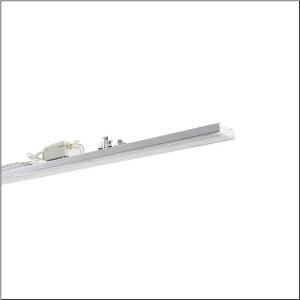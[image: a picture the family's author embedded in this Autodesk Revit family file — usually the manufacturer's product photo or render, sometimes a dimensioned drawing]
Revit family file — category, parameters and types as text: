
# Revit family: licross_r__21_recessed_ho_52te1ecn4cxs_0519
name_source: partatom
category: Lighting Fixtures
units: mm (PartAtom-declared; Revit-internal decimal feet)

## family parameters
Cut with Voids When Loaded = No
Host = Face
Light Source = No
Part Type = Normal
Room Calculation Point = No
Round Connector Dimension = Use Diameter
Shared = No

## types (1)
- --- (1 x LED, 12350 lm, 68.4 W, 4000K)
    Apparent Load = 68 VA
    CIE Flux Codes = 85 95 99 100 100
    Color Rendering = 80
    Color Temperature = 4000K
    Default Elevation = 1800 mm
    Description = Licross® 21 Recessed HO, luminaire insert, of sheet steel, galvanised, coil coated, white, length: 1.500mm, width: 66mm, height: 67mm, LED rated luminous flux: 12.350lm, light colour: 840, control gear: ON/OFF Multilumen, CLOi, control gear: ECG Multilumen, with plug, 3-pole, with phase selection, mains connection: 220..240V, AC, 50/60Hz, start of lifetime: 69W, end of service life: 83W, halogen-free wiring, primary light control with lens, of plastic, primary optical cover: cover, of PMMA, light emission: direct distribution, primary light characteristic: symmetric, protection rating (complete): IP54, insulation class (complete): insulation class I (protective earthing), certification: CE, ENEC, VDE, UKCA, protection symbol: D if used in an environment with non-conductive dust loads with corresponding accessories, impact resistance: IK06, permissible ambient temperature for indoor applications: -35..+30°C, corresponds to IFS (International Featured Standards) requirements for safety and quality in the food industry, reducing of maximum allowable ambient temperature of 5°C with ceiling mounting, LABS conformity tested according to VDMA 24364:2018-05, packaging unit: 1 piece
    Height = 58 mm
    Lamp = 1 x LED
    Lamp Light Flux = 12350 lm
    Lamp Power = 68.4 W
    Lamp count = 1
    Length = 1500 mm
    Luminous efficacy = 181 lm/W
    Manufacturer = Siteco
    ModVariant = No
    Model = 52TE1ECN4CXS
    Mounting Place = Ceiling
    Mounting Type = Pendant
    Number of Poles = 1
    OnlyDefault = Yes
    Power Factor = 1
    Product Name = Licross® 21 Recessed HO
    Product group = luminaire insert
    ProductGroupID = 901
    Protection Class = Protection class I
    Protection Degree = IP 54
    RLX_Detail_Level = 1
    RLX_Emergency_Light_Flux = 0 lm
    RLX_Emergency_Type = 0
    RLX_Emergency_Type_DB = No
    RlxData = <blob elided: 22469 chars, md5=0a83620f>
    Socket = socket
    Standby Power = 0 W
    System Light Flux = 12350 lm
    System Power = 68 W
    Type Comments = factory setting: luminous flux: 100 % | (A | C | E) | 161 mA
    Type Image = l_1296930.jpg
    URL = http://relux.com
    VarID = @adj_040033
    Voltage = 0 V
    Weight = 0.00 kg
    Width = 66 mm

## geometry (parser evidence)
native form markers: Blend x4, Sweep x10
no freeform markers — native parametric forms only
